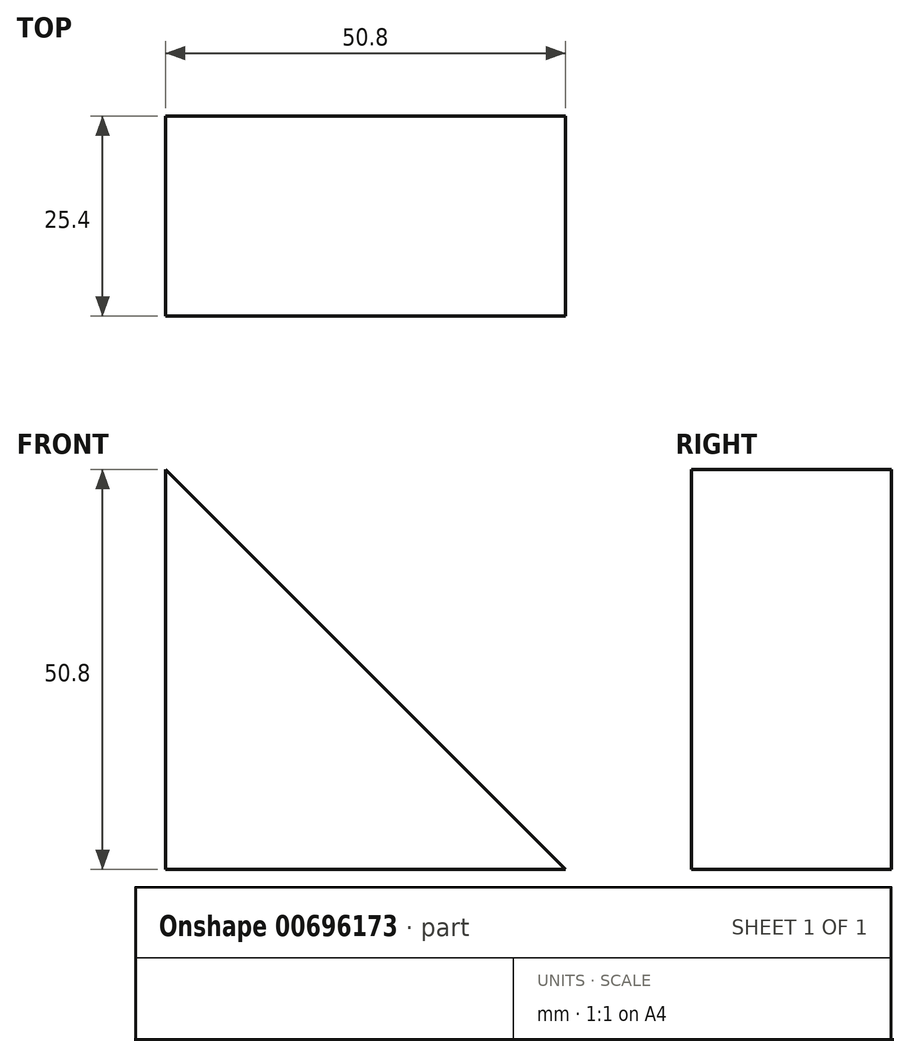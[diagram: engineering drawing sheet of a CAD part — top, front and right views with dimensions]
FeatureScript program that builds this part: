
annotation { "Feature Type Name" : "Feature", "Feature Type Description" : "" }
export const myFeature = defineFeature(function(context is Context, id is Id, definition is map)
    precondition{}
    {
        {
            var Q0;
            Q0=qCreatedBy(makeId("Front.planeOp"),FACE);
            var sketch = newSketch(context, id + "F0", { "sketchPlane" : qUnion([Q0])});
            skLineSegment(sketch, "E0", {"start": v(-38.86, 50.8) * mm, "end": v(-38.86, 0) * mm});
            skLineSegment(sketch, "E1", {"start": v(-38.86, 0) * mm, "end": v(11.94, 0) * mm});
            skLineSegment(sketch, "E2", {"start": v(-38.86, 50.8) * mm, "end": v(11.94, 0) * mm});
            skSolve(sketch);
        }
        {
            var Q0;
            Q0=makeQuery(id+"F0.imprint","IMPRINT",FACE,{"disambiguationData":[TD([[makeQuery(id+"F0.imprint","IMPRINT",EDGE,{"derivedFrom":sQuery(id+"F0.wireOp",EDGE,"E0")}),1.0]])]});
            extrude(context, id + "F1", {"entities" : qUnion([Q0]), "depth" : 25.4 * mm, "offsetDistance" : 25.4 * mm});
        }
    });
